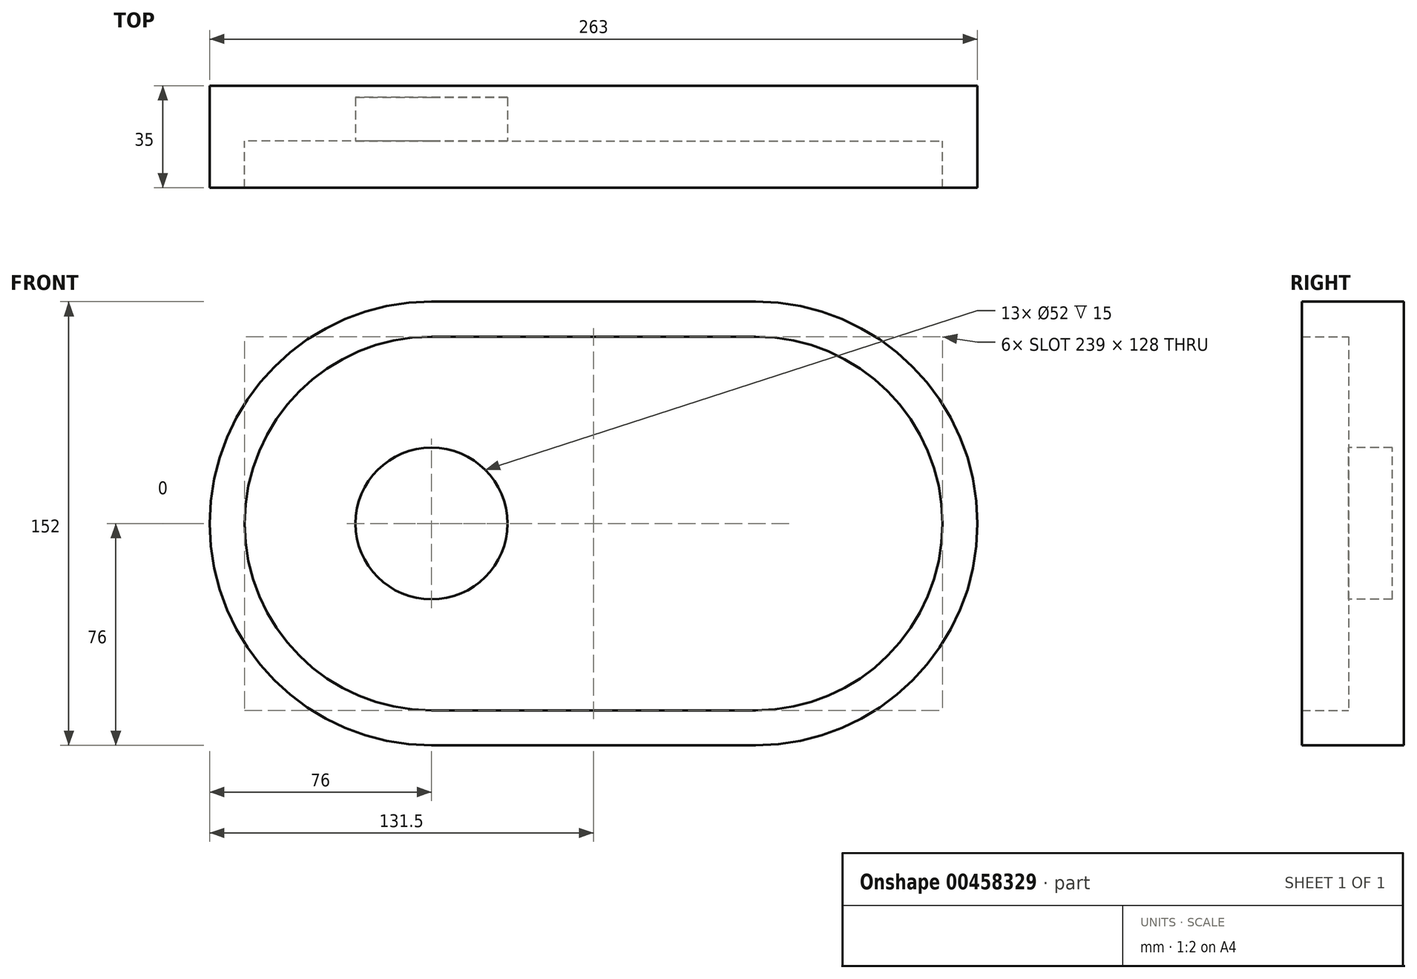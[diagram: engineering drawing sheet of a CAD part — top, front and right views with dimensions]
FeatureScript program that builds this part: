
annotation { "Feature Type Name" : "Feature", "Feature Type Description" : "" }
export const myFeature = defineFeature(function(context is Context, id is Id, definition is map)
    precondition{}
    {
        {
            var Q0;
            Q0=qCreatedBy(makeId("Front.planeOp"),FACE);
            var sketch = newSketch(context, id + "F0", { "sketchPlane" : qUnion([Q0])});
            skArc(sketch, "E0", {"start": v(0, 76) * mm, "mid": v(-76, 0) * mm, "end": v(0, -76) * mm});
            skLineSegment(sketch, "E1", {"start": v(0, 0) * mm, "end": v(111, 0) * mm});
            skArc(sketch, "E2", {"start": v(111, -76) * mm, "mid": v(187, 0) * mm, "end": v(111, 76) * mm});
            skLineSegment(sketch, "E3", {"start": v(0, 76) * mm, "end": v(111, 76) * mm});
            skLineSegment(sketch, "E4", {"start": v(0, -76) * mm, "end": v(111, -76) * mm});
            skSolve(sketch);
        }
        {
            var Q0;
            Q0=makeQuery(id+"F0.imprint","IMPRINT",FACE,{"disambiguationData":[TD([[makeQuery(id+"F0.imprint","IMPRINT",EDGE,{"derivedFrom":sQuery(id+"F0.wireOp",EDGE,"E0")}),1.0]])]});
            extrude(context, id + "F1", {"entities" : qUnion([Q0]), "depth" : 35 * mm, "offsetDistance" : 25 * mm});
        }
        {
            var Q0;
            Q0=qCreatedBy(makeId("Front.planeOp"),FACE);
            cPlane(context, id + "F2", {"entities" : qUnion([Q0]), "cplaneType" : CPlaneType.OFFSET, "offset" : 19 * mm, "width" : 150 * mm, "height" : 150 * mm});
        }
        {
            var Q0;
            Q0=qCreatedBy(id+"F2.planeOp",FACE);
            var sketch = newSketch(context, id + "F3", { "sketchPlane" : qUnion([Q0])});
            skArc(sketch, "E5", {"start": v(0, 64) * mm, "mid": v(-64, 0) * mm, "end": v(0, -64) * mm});
            skLineSegment(sketch, "E6", {"start": v(0, 0) * mm, "end": v(111, 0) * mm});
            skArc(sketch, "E7", {"start": v(111, -64) * mm, "mid": v(175, 0) * mm, "end": v(111, 64) * mm});
            skLineSegment(sketch, "E8", {"start": v(0, 64) * mm, "end": v(111, 64) * mm});
            skLineSegment(sketch, "E9", {"start": v(0, -64) * mm, "end": v(111, -64) * mm});
            skSolve(sketch);
        }
        {
            var Q0;
            Q0 = qSketchRegion(id + "F3", true);
            extrude(context, id + "F4", {"entities" : qUnion([Q0]), "operationType" : NewBodyOperationType.REMOVE, "depth" : 19 * mm, "offsetDistance" : 25 * mm});
        }
        {
            var Q0;
            Q0=qCreatedBy(id+"F2.planeOp",FACE);
            var sketch = newSketch(context, id + "F5", { "sketchPlane" : qUnion([Q0])});
            skCircle(sketch, "E10", {"center": v(0, 0) * mm, "radius": 26 * mm});
            skSolve(sketch);
        }
        {
            var Q0;
            Q0=makeQuery(id+"F5.imprint","IMPRINT",FACE,{"disambiguationData":[TD([[makeQuery(id+"F5.imprint","IMPRINT",EDGE,{"derivedFrom":sQuery(id+"F5.wireOp",EDGE,"E10")}),1.0]])]});
            extrude(context, id + "F6", {"entities" : qUnion([Q0]), "operationType" : NewBodyOperationType.REMOVE, "oppositeDirection" : true, "depth" : 15 * mm, "offsetDistance" : 25 * mm});
        }
    });
